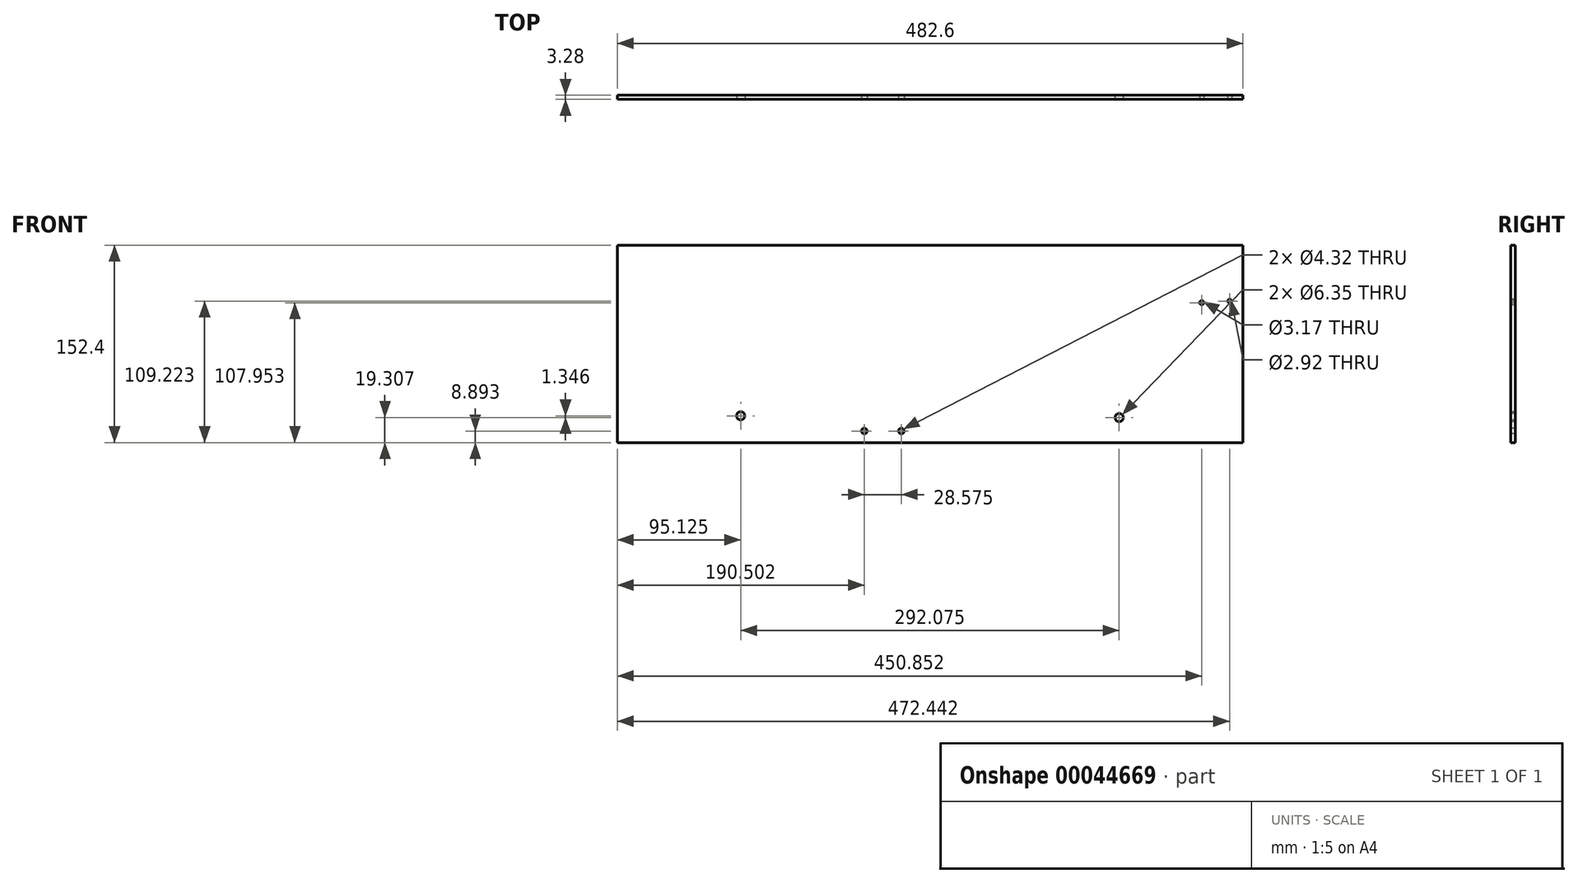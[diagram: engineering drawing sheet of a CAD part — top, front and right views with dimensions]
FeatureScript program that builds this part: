
annotation { "Feature Type Name" : "Feature", "Feature Type Description" : "" }
export const myFeature = defineFeature(function(context is Context, id is Id, definition is map)
    precondition{}
    {
        {
            var Q0;
            Q0=qCreatedBy(makeId("Front.planeOp"),FACE);
            var sketch = newSketch(context, id + "F0", { "sketchPlane" : qUnion([Q0])});
            skLineSegment(sketch, "E0.bottom", {"start": v(-227.54, 45.23) * mm, "end": v(255.06, 45.23) * mm});
            skLineSegment(sketch, "E0.top", {"start": v(-227.54, -107.17) * mm, "end": v(255.06, -107.17) * mm});
            skLineSegment(sketch, "E0.left", {"start": v(-227.54, 45.23) * mm, "end": v(-227.54, -107.17) * mm});
            skLineSegment(sketch, "E0.right", {"start": v(255.06, 45.23) * mm, "end": v(255.06, -107.17) * mm});
            skSolve(sketch);
        }
        {
            var Q0;
            Q0=makeQuery(id+"F0.imprint","IMPRINT",FACE,{"disambiguationData":[TD([[makeQuery(id+"F0.imprint","IMPRINT",EDGE,{"derivedFrom":sQuery(id+"F0.wireOp",EDGE,"E0.bottom")}),-1.0]])]});
            extrude(context, id + "F1", {"entities" : qUnion([Q0]), "depth" : 3.28 * mm});
        }
        {
            var Q0;
            Q0=makeQuery(id+"F1.opExtrude","CAP_FACE",FACE,{"disambiguationData":[OSD([sQuery(id+"F0.wireOp",EDGE,"E0.bottom"),sQuery(id+"F0.wireOp",EDGE,"E0.top"),sQuery(id+"F0.wireOp",EDGE,"E0.left"),sQuery(id+"F0.wireOp",EDGE,"E0.right")])],"isStart":false});
            var sketch = newSketch(context, id + "F2", { "sketchPlane" : qUnion([Q0])});
            skPoint(sketch, "E1", {"position": v(-199.09, 35) * mm});
            skPoint(sketch, "E2", {"position": v(-138.49, 35) * mm});
            skPoint(sketch, "E3", {"position": v(-118.34, 38.6) * mm});
            skPoint(sketch, "E4", {"position": v(-71.96, 33.02) * mm});
            skSolve(sketch);
        }
        {
            var Q0;
            Q0=makeQuery(id+"F2.imprint","IMPRINT",FACE,{"disambiguationData":[TD([[makeQuery(id+"F2.imprint","IMPRINT",EDGE,{"derivedFrom":makeQuery(id+"F1.opExtrude","CAP_EDGE",EDGE,{"disambiguationData":[OSD([sQuery(id+"F0.wireOp",EDGE,"E0.bottom")])],"isStart":false})}),-1.0]])]});
            var sketch = newSketch(context, id + "F3", { "sketchPlane" : qUnion([Q0])});
            skPoint(sketch, "E5", {"position": v(-214.76, 0.78) * mm});
            skPoint(sketch, "E6", {"position": v(-178.62, 0.78) * mm});
            skPoint(sketch, "E7", {"position": v(-132.41, -86.52) * mm});
            skPoint(sketch, "E8", {"position": v(-40.21, -96.83) * mm});
            skPoint(sketch, "E9", {"position": v(-8.39, -96.83) * mm});
            skPoint(sketch, "E10", {"position": v(-27.51, -77.02) * mm});
            skPoint(sketch, "E11", {"position": v(159.66, -87.86) * mm});
            skPoint(sketch, "E12", {"position": v(223.31, 0.78) * mm});
            skSolve(sketch);
        }
        {
            var Q0;
            Q0=sQuery(id+"F3.wireOp",VERTEX,"E12");
            var Q1;
            Q1=makeQuery(id+"F1.opExtrude","SWEPT_BODY",BODY,{"disambiguationData":[OSD([sQuery(id+"F0.wireOp",EDGE,"E0.bottom"),sQuery(id+"F0.wireOp",EDGE,"E0.top"),sQuery(id+"F0.wireOp",EDGE,"E0.left"),sQuery(id+"F0.wireOp",EDGE,"E0.right")])]});
            hole(context, id + "F4", {"style" : HoleStyle.SIMPLE, "holeDiameter" : 3.17 * mm, "endStyle" : HoleEndStyle.THROUGH, "locations" : qUnion([Q0]), "scope" : qUnion([Q1])});
        }
        {
            var Q0;
            Q0=makeQuery(id+"F2.imprint","IMPRINT",FACE,{"disambiguationData":[TD([[makeQuery(id+"F2.imprint","IMPRINT",EDGE,{"derivedFrom":makeQuery(id+"F1.opExtrude","CAP_EDGE",EDGE,{"disambiguationData":[OSD([sQuery(id+"F0.wireOp",EDGE,"E0.bottom")])],"isStart":false})}),-1.0]])]});
            var sketch = newSketch(context, id + "F5", { "sketchPlane" : qUnion([Q0])});
            skPoint(sketch, "E13", {"position": v(-8.46, -98.28) * mm});
            skSolve(sketch);
        }
        {
            var Q0;
            Q0=sQuery(id+"F5.wireOp",VERTEX,"E13");
            var Q1;
            Q1=makeQuery(id+"F1.opExtrude","SWEPT_BODY",BODY,{"disambiguationData":[OSD([sQuery(id+"F0.wireOp",EDGE,"E0.bottom"),sQuery(id+"F0.wireOp",EDGE,"E0.top"),sQuery(id+"F0.wireOp",EDGE,"E0.left"),sQuery(id+"F0.wireOp",EDGE,"E0.right")])]});
            hole(context, id + "F6", {"style" : HoleStyle.SIMPLE, "holeDiameter" : 4.32 * mm, "endStyle" : HoleEndStyle.THROUGH, "locations" : qUnion([Q0]), "scope" : qUnion([Q1])});
        }
        {
            var Q0;
            Q0=makeQuery(id+"F2.imprint","IMPRINT",FACE,{"disambiguationData":[TD([[makeQuery(id+"F2.imprint","IMPRINT",EDGE,{"derivedFrom":makeQuery(id+"F1.opExtrude","CAP_EDGE",EDGE,{"disambiguationData":[OSD([sQuery(id+"F0.wireOp",EDGE,"E0.bottom")])],"isStart":false})}),-1.0]])]});
            var sketch = newSketch(context, id + "F7", { "sketchPlane" : qUnion([Q0])});
            skPoint(sketch, "E14", {"position": v(-37.04, -98.28) * mm});
            skSolve(sketch);
        }
        {
            var Q0;
            Q0=sQuery(id+"F7.wireOp",VERTEX,"E14");
            var Q1;
            Q1=makeQuery(id+"F1.opExtrude","SWEPT_BODY",BODY,{"disambiguationData":[OSD([sQuery(id+"F0.wireOp",EDGE,"E0.bottom"),sQuery(id+"F0.wireOp",EDGE,"E0.top"),sQuery(id+"F0.wireOp",EDGE,"E0.left"),sQuery(id+"F0.wireOp",EDGE,"E0.right")])]});
            hole(context, id + "F8", {"style" : HoleStyle.SIMPLE, "holeDiameter" : 4.32 * mm, "endStyle" : HoleEndStyle.THROUGH, "locations" : qUnion([Q0]), "scope" : qUnion([Q1])});
        }
        {
            var Q0;
            Q0=makeQuery(id+"F2.imprint","IMPRINT",FACE,{"disambiguationData":[TD([[makeQuery(id+"F2.imprint","IMPRINT",EDGE,{"derivedFrom":makeQuery(id+"F1.opExtrude","CAP_EDGE",EDGE,{"disambiguationData":[OSD([sQuery(id+"F0.wireOp",EDGE,"E0.bottom")])],"isStart":false})}),-1.0]])]});
            var sketch = newSketch(context, id + "F9", { "sketchPlane" : qUnion([Q0])});
            skPoint(sketch, "E15", {"position": v(244.9, 2.05) * mm});
            skSolve(sketch);
        }
        {
            var Q0;
            Q0=sQuery(id+"F9.wireOp",VERTEX,"E15");
            var Q1;
            Q1=makeQuery(id+"F1.opExtrude","SWEPT_BODY",BODY,{"disambiguationData":[OSD([sQuery(id+"F0.wireOp",EDGE,"E0.bottom"),sQuery(id+"F0.wireOp",EDGE,"E0.top"),sQuery(id+"F0.wireOp",EDGE,"E0.left"),sQuery(id+"F0.wireOp",EDGE,"E0.right")])]});
            hole(context, id + "F10", {"style" : HoleStyle.SIMPLE, "holeDiameter" : 2.92 * mm, "endStyle" : HoleEndStyle.THROUGH, "locations" : qUnion([Q0]), "scope" : qUnion([Q1])});
        }
        {
            var Q0;
            Q0=sQuery(id+"F3.wireOp",VERTEX,"E7");
            var Q1;
            Q1=sQuery(id+"F3.wireOp",VERTEX,"E11");
            var Q2;
            Q2=makeQuery(id+"F1.opExtrude","SWEPT_BODY",BODY,{"disambiguationData":[OSD([sQuery(id+"F0.wireOp",EDGE,"E0.bottom"),sQuery(id+"F0.wireOp",EDGE,"E0.top"),sQuery(id+"F0.wireOp",EDGE,"E0.left"),sQuery(id+"F0.wireOp",EDGE,"E0.right")])]});
            hole(context, id + "F11", {"style" : HoleStyle.SIMPLE, "holeDiameter" : 6.35 * mm, "endStyle" : HoleEndStyle.THROUGH, "locations" : qUnion([Q0, Q1]), "scope" : qUnion([Q2])});
        }
    });
